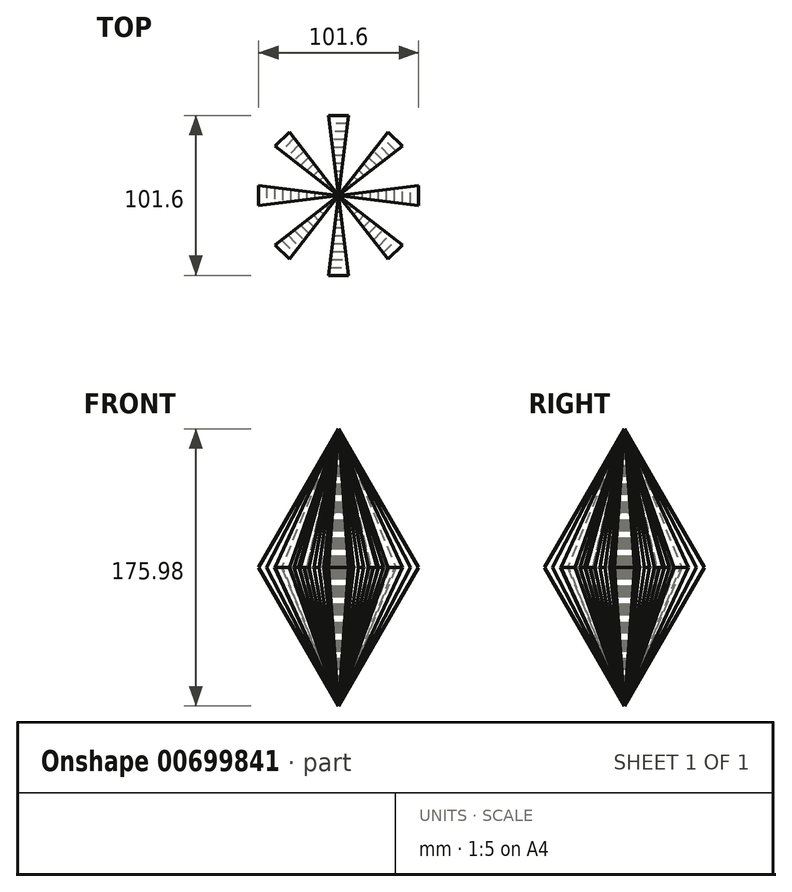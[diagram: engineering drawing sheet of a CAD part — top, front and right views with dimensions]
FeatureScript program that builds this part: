
annotation { "Feature Type Name" : "Feature", "Feature Type Description" : "" }
export const myFeature = defineFeature(function(context is Context, id is Id, definition is map)
    precondition{}
    {
        {
            var Q0;
            Q0=qCreatedBy(makeId("Front.planeOp"),FACE);
            var sketch = newSketch(context, id + "F0", { "sketchPlane" : qUnion([Q0])});
            skLineSegment(sketch, "E0", {"start": v(0, 0) * mm, "end": v(50.8, 87.99) * mm});
            skLineSegment(sketch, "E1", {"start": v(50.8, 87.99) * mm, "end": v(0, 175.98) * mm});
            skLineSegment(sketch, "E2", {"start": v(0, 175.98) * mm, "end": v(-50.8, 87.99) * mm});
            skLineSegment(sketch, "E3", {"start": v(-50.8, 87.99) * mm, "end": v(0, 0) * mm});
            skLineSegment(sketch, "E4", {"start": v(0, 175.98) * mm, "end": v(0, 0) * mm});
            skLineSegment(sketch, "E5", {"start": v(0, 87.99) * mm, "end": v(50.8, 87.99) * mm});
            skPoint(sketch, "E6", {"position": v(45.72, 87.99) * mm});
            skPoint(sketch, "E7.1.0.0", {"position": v(40.64, 87.99) * mm});
            skPoint(sketch, "E7.2.0.0", {"position": v(35.56, 87.99) * mm});
            skPoint(sketch, "E7.3.0.0", {"position": v(30.48, 87.99) * mm});
            skPoint(sketch, "E7.4.0.0", {"position": v(25.4, 87.99) * mm});
            skPoint(sketch, "E7.5.0.0", {"position": v(20.32, 87.99) * mm});
            skPoint(sketch, "E7.6.0.0", {"position": v(15.24, 87.99) * mm});
            skPoint(sketch, "E7.7.0.0", {"position": v(10.16, 87.99) * mm});
            skPoint(sketch, "E7.8.0.0", {"position": v(5.08, 87.99) * mm});
            skLineSegment(sketch, "E7.direction1", {"start": v(45.72, 87.99) * mm, "end": v(40.64, 87.99) * mm, "construction": true});
            skLineSegment(sketch, "E8", {"start": v(0, 175.98) * mm, "end": v(45.72, 87.99) * mm});
            skLineSegment(sketch, "E9", {"start": v(0, 0) * mm, "end": v(0, 0) * mm});
            skLineSegment(sketch, "E10", {"start": v(45.72, 87.99) * mm, "end": v(0, 0) * mm});
            skLineSegment(sketch, "E11", {"start": v(40.64, 87.99) * mm, "end": v(0, 0) * mm});
            skLineSegment(sketch, "E12", {"start": v(35.56, 87.99) * mm, "end": v(40.64, 87.99) * mm});
            skLineSegment(sketch, "E13", {"start": v(40.64, 87.99) * mm, "end": v(0, 175.98) * mm});
            skLineSegment(sketch, "E14", {"start": v(0, 175.98) * mm, "end": v(35.56, 87.99) * mm});
            skLineSegment(sketch, "E15", {"start": v(30.48, 87.99) * mm, "end": v(0, 175.98) * mm});
            skLineSegment(sketch, "E16", {"start": v(25.4, 87.99) * mm, "end": v(0, 175.98) * mm});
            skLineSegment(sketch, "E17", {"start": v(0, 175.98) * mm, "end": v(20.32, 87.99) * mm});
            skLineSegment(sketch, "E18", {"start": v(0, 175.98) * mm, "end": v(15.24, 87.99) * mm});
            skLineSegment(sketch, "E19", {"start": v(10.16, 87.99) * mm, "end": v(0, 175.98) * mm});
            skLineSegment(sketch, "E20", {"start": v(5.08, 87.99) * mm, "end": v(0, 175.98) * mm});
            skLineSegment(sketch, "E21", {"start": v(5.08, 87.99) * mm, "end": v(0, 0) * mm});
            skLineSegment(sketch, "E22", {"start": v(0, 0) * mm, "end": v(10.16, 87.99) * mm});
            skLineSegment(sketch, "E23", {"start": v(15.24, 87.99) * mm, "end": v(0, 0) * mm});
            skLineSegment(sketch, "E24", {"start": v(20.32, 87.99) * mm, "end": v(0, 0) * mm});
            skLineSegment(sketch, "E25", {"start": v(25.4, 87.99) * mm, "end": v(0, 0) * mm});
            skLineSegment(sketch, "E26", {"start": v(30.48, 87.99) * mm, "end": v(0, 0) * mm});
            skLineSegment(sketch, "E27", {"start": v(35.56, 87.99) * mm, "end": v(35.56, 87.99) * mm});
            skLineSegment(sketch, "E28", {"start": v(0, 0) * mm, "end": v(35.56, 87.99) * mm});
            skLineSegment(sketch, "E29", {"start": v(0, 87.99) * mm, "end": v(5.08, 87.99) * mm});
            skLineSegment(sketch, "E30", {"start": v(5.08, 87.99) * mm, "end": v(10.16, 87.99) * mm});
            skLineSegment(sketch, "E31", {"start": v(10.16, 87.99) * mm, "end": v(15.24, 87.99) * mm});
            skLineSegment(sketch, "E32", {"start": v(15.24, 87.99) * mm, "end": v(20.32, 87.99) * mm});
            skLineSegment(sketch, "E33", {"start": v(20.32, 87.99) * mm, "end": v(25.4, 87.99) * mm});
            skLineSegment(sketch, "E34", {"start": v(25.4, 87.99) * mm, "end": v(30.48, 87.99) * mm});
            skLineSegment(sketch, "E35", {"start": v(30.48, 87.99) * mm, "end": v(35.56, 87.99) * mm});
            skLineSegment(sketch, "E36", {"start": v(40.64, 87.99) * mm, "end": v(45.72, 87.99) * mm});
            skLineSegment(sketch, "E37", {"start": v(45.72, 87.99) * mm, "end": v(50.8, 87.99) * mm});
            skSolve(sketch);
        }
        {
            var Q0;
            Q0=makeQuery(id+"F0.imprint","IMPRINT",FACE,{"disambiguationData":[TD([[makeQuery(id+"F0.imprint","IMPRINT",EDGE,{"derivedFrom":sQuery(id+"F0.wireOp",EDGE,"E21")}),1.0]])]});
            var Q1;
            Q1=makeQuery(id+"F0.imprint","IMPRINT",FACE,{"disambiguationData":[TD([[makeQuery(id+"F0.imprint","IMPRINT",EDGE,{"derivedFrom":sQuery(id+"F0.wireOp",EDGE,"E19")}),1.0]])]});
            var Q2;
            Q2=makeQuery(id+"F0.imprint","IMPRINT",FACE,{"disambiguationData":[TD([[makeQuery(id+"F0.imprint","IMPRINT",EDGE,{"derivedFrom":sQuery(id+"F0.wireOp",EDGE,"E23")}),1.0]])]});
            var Q3;
            Q3=makeQuery(id+"F0.imprint","IMPRINT",FACE,{"disambiguationData":[TD([[makeQuery(id+"F0.imprint","IMPRINT",EDGE,{"derivedFrom":sQuery(id+"F0.wireOp",EDGE,"E17")}),-1.0]])]});
            var Q4;
            Q4=makeQuery(id+"F0.imprint","IMPRINT",FACE,{"disambiguationData":[TD([[makeQuery(id+"F0.imprint","IMPRINT",EDGE,{"derivedFrom":sQuery(id+"F0.wireOp",EDGE,"E15")}),1.0]])]});
            var Q5;
            Q5=makeQuery(id+"F0.imprint","IMPRINT",FACE,{"disambiguationData":[TD([[makeQuery(id+"F0.imprint","IMPRINT",EDGE,{"derivedFrom":sQuery(id+"F0.wireOp",EDGE,"E25")}),1.0]])]});
            var Q6;
            Q6=makeQuery(id+"F0.imprint","IMPRINT",FACE,{"disambiguationData":[TD([[makeQuery(id+"F0.imprint","IMPRINT",EDGE,{"derivedFrom":sQuery(id+"F0.wireOp",EDGE,"E12")}),1.0]])]});
            var Q7;
            Q7=makeQuery(id+"F0.imprint","IMPRINT",FACE,{"disambiguationData":[TD([[makeQuery(id+"F0.imprint","IMPRINT",EDGE,{"derivedFrom":sQuery(id+"F0.wireOp",EDGE,"E11")}),-1.0]])]});
            var Q8;
            Q8=makeQuery(id+"F0.imprint","IMPRINT",FACE,{"disambiguationData":[TD([[makeQuery(id+"F0.imprint","IMPRINT",EDGE,{"derivedFrom":sQuery(id+"F0.wireOp",EDGE,"E1")}),1.0]])]});
            var Q9;
            Q9=makeQuery(id+"F0.imprint","IMPRINT",FACE,{"disambiguationData":[TD([[makeQuery(id+"F0.imprint","IMPRINT",EDGE,{"derivedFrom":sQuery(id+"F0.wireOp",EDGE,"E0")}),1.0]])]});
            extrude(context, id + "F1", {"entities" : qUnion([Q0, Q1, Q2, Q3, Q4, Q5, Q6, Q7, Q8, Q9]), "endBound" : BoundingType.SYMMETRIC, "depth" : 12.7 * mm, "offsetDistance" : 25.4 * mm});
        }
        {
            var Q0;
            Q0=qCreatedBy(makeId("Top.planeOp"),FACE);
            var sketch = newSketch(context, id + "F2", { "sketchPlane" : qUnion([Q0])});
            skLineSegment(sketch, "E38", {"start": v(0, 0) * mm, "end": v(0, 6.35) * mm});
            skLineSegment(sketch, "E39", {"start": v(0, -6.35) * mm, "end": v(50.8, -6.35) * mm});
            skLineSegment(sketch, "E40", {"start": v(50.8, -6.35) * mm, "end": v(50.8, 0) * mm});
            skLineSegment(sketch, "E41", {"start": v(50.8, 0) * mm, "end": v(50.8, 6.35) * mm});
            skLineSegment(sketch, "E42", {"start": v(50.8, 6.35) * mm, "end": v(0, 6.35) * mm});
            skPoint(sketch, "E43.orphan", {"position": v(0, 175.98) * mm});
            skLineSegment(sketch, "E44", {"start": v(0, 0) * mm, "end": v(0, -6.35) * mm});
            skLineSegment(sketch, "E45", {"start": v(50.8, 6.35) * mm, "end": v(0, 0) * mm});
            skLineSegment(sketch, "E46", {"start": v(50.8, -6.35) * mm, "end": v(0, 0) * mm});
            skSolve(sketch);
        }
        {
            var Q0;
            Q0=makeQuery(id+"F2.imprint","IMPRINT",FACE,{"disambiguationData":[TD([[makeQuery(id+"F2.imprint","IMPRINT",EDGE,{"derivedFrom":sQuery(id+"F2.wireOp",EDGE,"E38")}),-1.0]])]});
            var Q1;
            Q1=makeQuery(id+"F2.imprint","IMPRINT",FACE,{"disambiguationData":[TD([[makeQuery(id+"F2.imprint","IMPRINT",EDGE,{"derivedFrom":sQuery(id+"F2.wireOp",EDGE,"E39")}),1.0]])]});
            extrude(context, id + "F3", {"entities" : qUnion([Q0, Q1]), "operationType" : NewBodyOperationType.REMOVE, "endBound" : BoundingType.THROUGH_ALL, "depth" : 25.4 * mm, "offsetDistance" : 25.4 * mm});
        }
        {
            var Q0;
            Q0=qCreatedBy(makeId("Top.planeOp"),FACE);
            var sketch = newSketch(context, id + "F4", { "sketchPlane" : qUnion([Q0])});
            skLineSegment(sketch, "E47", {"start": v(0, 0) * mm, "end": v(50.8, -13.97) * mm});
            skLineSegment(sketch, "E48", {"start": v(50.8, -13.97) * mm, "end": v(50.8, 13.97) * mm});
            skLineSegment(sketch, "E49", {"start": v(50.8, 13.97) * mm, "end": v(0, 0) * mm});
            skLineSegment(sketch, "E50", {"start": v(50.8, -13.97) * mm, "end": v(0, -13.97) * mm});
            skLineSegment(sketch, "E51", {"start": v(0, -13.97) * mm, "end": v(0, 13.97) * mm});
            skLineSegment(sketch, "E52", {"start": v(0, 13.97) * mm, "end": v(50.8, 13.97) * mm});
            skSolve(sketch);
        }
        {
            var Q0;
            {var subQ0=sQuery(id+"F4.wireOp",EDGE,"E47");Q0=makeQuery(id+"F4.imprint","IMPRINT",FACE,{"disambiguationData":[TD([[makeQuery(id+"F4.imprint","IMPRINT",EDGE,{"derivedFrom":subQ0}),-1.0]])]});}
            var Q1;
            {var subQ0=sQuery(id+"F4.wireOp",EDGE,"E49");Q1=makeQuery(id+"F4.imprint","IMPRINT",FACE,{"disambiguationData":[TD([[makeQuery(id+"F4.imprint","IMPRINT",EDGE,{"derivedFrom":subQ0}),-1.0]])]});}
            var Q2;
            Q2 = qSketchRegion(id + "F6", true);
            extrude(context, id + "F5", {"entities" : qUnion([Q0, Q1, Q2]), "operationType" : NewBodyOperationType.REMOVE, "endBound" : BoundingType.THROUGH_ALL, "depth" : 25.4 * mm, "offsetDistance" : 25.4 * mm});
        }
        {
            var Q0;
            Q0=qCreatedBy(makeId("Front.planeOp"),FACE);
            var sketch = newSketch(context, id + "F6", { "sketchPlane" : qUnion([Q0])});
            skLineSegment(sketch, "E53", {"start": v(0, 87.99) * mm, "end": v(50.8, 87.99) * mm});
            skLineSegment(sketch, "E54", {"start": v(50.8, 87.99) * mm, "end": v(0, 175.98) * mm});
            skLineSegment(sketch, "E55", {"start": v(0, 175.98) * mm, "end": v(0, 0) * mm});
            skLineSegment(sketch, "E56", {"start": v(0, 0) * mm, "end": v(50.8, 87.99) * mm});
            skPoint(sketch, "E57", {"position": v(45.72, 87.99) * mm});
            skPoint(sketch, "E58.1.0.0", {"position": v(40.64, 87.99) * mm});
            skPoint(sketch, "E58.2.0.0", {"position": v(35.56, 87.99) * mm});
            skPoint(sketch, "E58.3.0.0", {"position": v(30.48, 87.99) * mm});
            skPoint(sketch, "E58.4.0.0", {"position": v(25.4, 87.99) * mm});
            skPoint(sketch, "E58.5.0.0", {"position": v(20.32, 87.99) * mm});
            skPoint(sketch, "E58.6.0.0", {"position": v(15.24, 87.99) * mm});
            skPoint(sketch, "E58.7.0.0", {"position": v(10.16, 87.99) * mm});
            skPoint(sketch, "E58.8.0.0", {"position": v(5.08, 87.99) * mm});
            skLineSegment(sketch, "E58.direction1", {"start": v(45.72, 87.99) * mm, "end": v(40.64, 87.99) * mm, "construction": true});
            skLineSegment(sketch, "E59", {"start": v(0, 175.98) * mm, "end": v(45.72, 87.99) * mm});
            skLineSegment(sketch, "E60", {"start": v(0, 0) * mm, "end": v(0, 0) * mm});
            skLineSegment(sketch, "E61", {"start": v(45.72, 87.99) * mm, "end": v(0, 0) * mm});
            skLineSegment(sketch, "E62", {"start": v(40.64, 87.99) * mm, "end": v(0, 0) * mm});
            skLineSegment(sketch, "E63", {"start": v(35.56, 87.99) * mm, "end": v(40.64, 87.99) * mm});
            skLineSegment(sketch, "E64", {"start": v(40.64, 87.99) * mm, "end": v(0, 175.98) * mm});
            skLineSegment(sketch, "E65", {"start": v(0, 175.98) * mm, "end": v(35.56, 87.99) * mm});
            skLineSegment(sketch, "E66", {"start": v(30.48, 87.99) * mm, "end": v(0, 175.98) * mm});
            skLineSegment(sketch, "E67", {"start": v(25.4, 87.99) * mm, "end": v(0, 175.98) * mm});
            skLineSegment(sketch, "E68", {"start": v(0, 175.98) * mm, "end": v(20.32, 87.99) * mm});
            skLineSegment(sketch, "E69", {"start": v(0, 175.98) * mm, "end": v(15.24, 87.99) * mm});
            skLineSegment(sketch, "E70", {"start": v(10.16, 87.99) * mm, "end": v(0, 175.98) * mm});
            skLineSegment(sketch, "E71", {"start": v(5.08, 87.99) * mm, "end": v(0, 175.98) * mm});
            skLineSegment(sketch, "E72", {"start": v(5.08, 87.99) * mm, "end": v(0, 0) * mm});
            skLineSegment(sketch, "E73", {"start": v(0, 0) * mm, "end": v(10.16, 87.99) * mm});
            skLineSegment(sketch, "E74", {"start": v(15.24, 87.99) * mm, "end": v(0, 0) * mm});
            skLineSegment(sketch, "E75", {"start": v(20.32, 87.99) * mm, "end": v(0, 0) * mm});
            skLineSegment(sketch, "E76", {"start": v(25.4, 87.99) * mm, "end": v(0, 0) * mm});
            skLineSegment(sketch, "E77", {"start": v(30.48, 87.99) * mm, "end": v(0, 0) * mm});
            skLineSegment(sketch, "E78", {"start": v(35.56, 87.99) * mm, "end": v(35.56, 87.99) * mm});
            skLineSegment(sketch, "E79", {"start": v(0, 0) * mm, "end": v(35.56, 87.99) * mm});
            skLineSegment(sketch, "E80", {"start": v(0, 87.99) * mm, "end": v(5.08, 87.99) * mm});
            skLineSegment(sketch, "E81", {"start": v(5.08, 87.99) * mm, "end": v(10.16, 87.99) * mm});
            skLineSegment(sketch, "E82", {"start": v(10.16, 87.99) * mm, "end": v(15.24, 87.99) * mm});
            skLineSegment(sketch, "E83", {"start": v(15.24, 87.99) * mm, "end": v(20.32, 87.99) * mm});
            skLineSegment(sketch, "E84", {"start": v(20.32, 87.99) * mm, "end": v(25.4, 87.99) * mm});
            skLineSegment(sketch, "E85", {"start": v(25.4, 87.99) * mm, "end": v(30.48, 87.99) * mm});
            skLineSegment(sketch, "E86", {"start": v(30.48, 87.99) * mm, "end": v(35.56, 87.99) * mm});
            skLineSegment(sketch, "E87", {"start": v(40.64, 87.99) * mm, "end": v(45.72, 87.99) * mm});
            skLineSegment(sketch, "E88", {"start": v(45.72, 87.99) * mm, "end": v(50.8, 87.99) * mm});
            skSolve(sketch);
        }
        {
            var Q0;
            Q0=makeQuery(id+"F2.imprint","IMPRINT",FACE,{"disambiguationData":[TD([[makeQuery(id+"F2.imprint","IMPRINT",EDGE,{"derivedFrom":sQuery(id+"F2.wireOp",EDGE,"E39")}),1.0]])]});
            var Q1;
            Q1=makeQuery(id+"F2.imprint","IMPRINT",FACE,{"disambiguationData":[TD([[makeQuery(id+"F2.imprint","IMPRINT",EDGE,{"derivedFrom":sQuery(id+"F2.wireOp",EDGE,"E38")}),-1.0]])]});
            extrude(context, id + "F7", {"entities" : qUnion([Q0, Q1]), "operationType" : NewBodyOperationType.REMOVE, "endBound" : BoundingType.THROUGH_ALL, "depth" : 25.4 * mm, "offsetDistance" : 25.4 * mm});
        }
        {
            var Q0;
            Q0=makeQuery(id+"F1.opExtrude","SWEPT_BODY",BODY,{"disambiguationData":[OSD([sQuery(id+"F0.wireOp",EDGE,"E19"),sQuery(id+"F0.wireOp",EDGE,"E20"),sQuery(id+"F0.wireOp",EDGE,"E21"),sQuery(id+"F0.wireOp",EDGE,"E22")])]});
            var Q1;
            Q1=sQuery(id+"F0.wireOp",EDGE,"E4");
            circularPattern(context, id + "F8", {"entities" : qUnion([Q0]), "axis" : qUnion([Q1]), "angle" : 360 * degree, "instanceCount" : 8, "equalSpace" : true});
        }
        {
            var Q0;
            Q0=makeQuery(id+"F1.opExtrude","SWEPT_BODY",BODY,{"disambiguationData":[OSD([sQuery(id+"F0.wireOp",EDGE,"E17"),sQuery(id+"F0.wireOp",EDGE,"E18"),sQuery(id+"F0.wireOp",EDGE,"E23"),sQuery(id+"F0.wireOp",EDGE,"E24")])]});
            var Q1;
            Q1=sQuery(id+"F0.wireOp",EDGE,"E4");
            circularPattern(context, id + "F9", {"entities" : qUnion([Q0]), "axis" : qUnion([Q1]), "angle" : 360 * degree, "instanceCount" : 8, "equalSpace" : true});
        }
        {
            var Q0;
            Q0=makeQuery(id+"F1.opExtrude","SWEPT_BODY",BODY,{"disambiguationData":[OSD([sQuery(id+"F0.wireOp",EDGE,"E15"),sQuery(id+"F0.wireOp",EDGE,"E16"),sQuery(id+"F0.wireOp",EDGE,"E25"),sQuery(id+"F0.wireOp",EDGE,"E26")])]});
            var Q1;
            Q1=sQuery(id+"F0.wireOp",EDGE,"E4");
            circularPattern(context, id + "F10", {"entities" : qUnion([Q0]), "axis" : qUnion([Q1]), "angle" : 360 * degree, "instanceCount" : 8, "equalSpace" : true});
        }
        {
            var Q0;
            Q0=makeQuery(id+"F1.opExtrude","SWEPT_BODY",BODY,{"disambiguationData":[OSD([sQuery(id+"F0.wireOp",EDGE,"E11"),sQuery(id+"F0.wireOp",EDGE,"E13"),sQuery(id+"F0.wireOp",EDGE,"E14"),sQuery(id+"F0.wireOp",EDGE,"E28")])]});
            var Q1;
            Q1=sQuery(id+"F0.wireOp",EDGE,"E4");
            circularPattern(context, id + "F11", {"entities" : qUnion([Q0]), "axis" : qUnion([Q1]), "angle" : 360 * degree, "instanceCount" : 8, "equalSpace" : true});
        }
        {
            var Q0;
            Q0=makeQuery(id+"F1.opExtrude","SWEPT_BODY",BODY,{"disambiguationData":[OSD([sQuery(id+"F0.wireOp",EDGE,"E1"),sQuery(id+"F0.wireOp",EDGE,"E0"),sQuery(id+"F0.wireOp",EDGE,"E8"),sQuery(id+"F0.wireOp",EDGE,"E10")])]});
            var Q1;
            Q1=sQuery(id+"F0.wireOp",EDGE,"E4");
            circularPattern(context, id + "F12", {"entities" : qUnion([Q0]), "axis" : qUnion([Q1]), "angle" : 360 * degree, "instanceCount" : 8, "equalSpace" : true});
        }
    });
